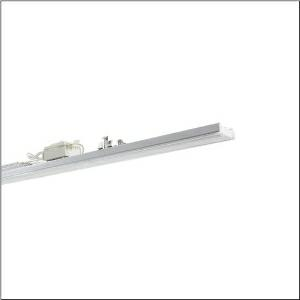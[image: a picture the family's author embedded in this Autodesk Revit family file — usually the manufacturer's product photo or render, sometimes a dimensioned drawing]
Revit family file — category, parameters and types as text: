
# Revit family: licross_r__21_recessed_ho_52tl12dn1e5m_37b9
name_source: partatom
category: Lighting Fixtures
units: mm (PartAtom-declared; Revit-internal decimal feet)

## family parameters
Cut with Voids When Loaded = No
Host = Face
Light Source = No
Part Type = Normal
Room Calculation Point = No
Round Connector Dimension = Use Diameter
Shared = No

## types (1)
- --- (1 x LED, 14510 lm, 84.6 W, 3500K)
    Apparent Load = 85 VA
    CIE Flux Codes = 69 91 98 100 100
    Color Rendering = 80
    Color Temperature = 3500K
    Default Elevation = 1800 mm
    Description = Licross® 21 Recessed HO, luminaire insert, of sheet steel, galvanised, coil coated, white, length: 1.500mm, width: 66mm, height: 67mm, LED rated luminous flux: 14.510lm, light colour: 835, control gear: DALI 2, with plug, 5-pole, with phase selection, mains connection: 220..240V, AC, 50/60Hz, rated input power: 85W, halogen-free wiring, primary optical cover: cover, of PMMA, light emission: direct distribution, primary light characteristic: symmetric, protection rating (complete): IP40, insulation class (complete): insulation class I (protective earthing), certification: CE, ENEC, VDE, UKCA, protection symbol: D if used in an environment without relevant dust loads with corresponding accessories, impact resistance: IK06, permissible ambient temperature for indoor applications: -25..+30°C, corresponds to IFS (International Featured Standards) requirements for safety and quality in the food industry, reducing of maximum allowable ambient temperature of 5°C with ceiling mounting, LABS conformity tested according to VDMA 24364:2018-05, packaging unit: 1 piece
    Height = 58 mm
    Lamp = 1 x LED
    Lamp Light Flux = 14510 lm
    Lamp Power = 84.6 W
    Lamp count = 1
    Length = 1500 mm
    Luminous efficacy = 172 lm/W
    Manufacturer = Siteco
    ModVariant = No
    Model = 52TL12DN1E5M
    Mounting Place = Ceiling
    Mounting Type = Pendant
    Number of Poles = 1
    OnlyDefault = Yes
    Power Factor = 1
    Product Name = Licross® 21 Recessed HO
    Product group = luminaire insert
    ProductGroupID = 902
    Protection Class = Protection class I
    Protection Degree = IP 40
    RLX_Detail_Level = 1
    RLX_Emergency_Light_Flux = 0 lm
    RLX_Emergency_Type = 0
    RLX_Emergency_Type_DB = No
    RlxData = <blob elided: 24665 chars, md5=bf045e4f>
    Socket = socket
    Standby Power = 0 W
    System Light Flux = 14510 lm
    System Power = 85 W
    Type Comments = factory setting: luminous flux: 100 % | dim-lin: 254 | 484 mA
    Type Image = l_1296930.jpg
    URL = http://relux.com
    VarID = @adj_089058
    Voltage = 0 V
    Weight = 0.00 kg
    Width = 66 mm

## geometry (parser evidence)
native form markers: Blend x4, Sweep x10
no freeform markers — native parametric forms only
